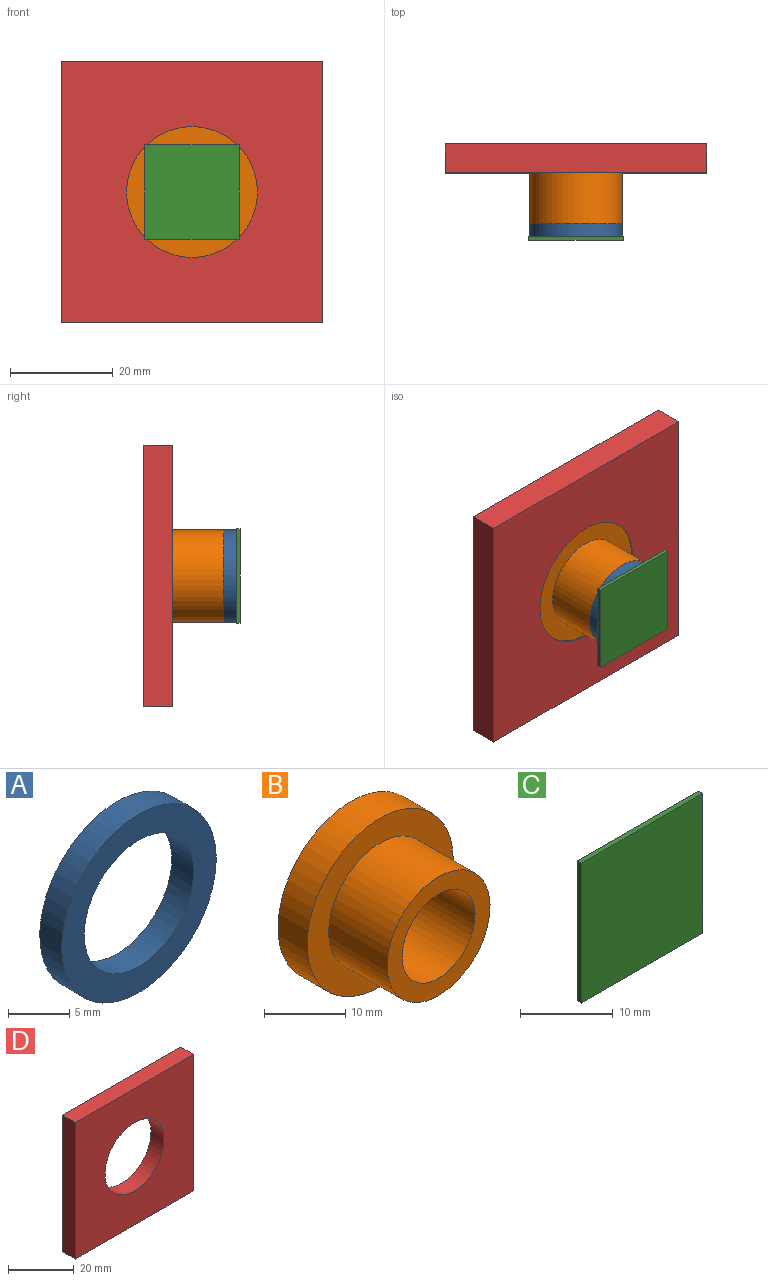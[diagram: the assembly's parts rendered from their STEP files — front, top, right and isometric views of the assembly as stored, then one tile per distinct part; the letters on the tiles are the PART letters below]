
ASSEMBLY  parts=4 mates=2
PART A: 4 faces, bbox 17.9x2.5x17.9 mm
  f0: cylinder r=6.35mm len=12.7mm, axis (0,1,0), area 101.3mm2, adj f2,f3
  f1: cylinder r=8.95mm len=17.91mm, axis (0,1,0), area 142.9mm2, adj f2,f3
  f2: plane 17.91x17.91mm, normal (0,-1,0), area 125.2mm2, adj f0,f1
  f3: plane 17.91x17.91mm, normal (0,1,0), area 125.2mm2, adj f0,f1
PART B: 6 faces, bbox 25.4x15.2x25.4 mm
  f0: cylinder r=12.7mm len=25.4mm, axis (0,1,0), area 405.4mm2, adj f1,f2
  f1: plane 25.4x25.4mm, normal (0,-1,0), area 254.9mm2, adj f0,f4
  f2: plane 25.4x25.4mm, normal (0,1,0), area 380mm2, adj f0,f3
  f3: cylinder r=6.35mm len=15.24mm, axis (0,1,0), area 608mm2, adj f2,f5
  f4: cylinder r=8.95mm len=17.91mm, axis (0,1,0), area 571.6mm2, adj f1,f5
  f5: plane 17.91x17.91mm, normal (0,-1,0), area 125.2mm2, adj f3,f4
PART C: 6 faces, bbox 18.4x0.6x18.4 mm
  f0: plane 18.42x0.64mm, normal (1,0,0), area 11.7mm2, adj f1,f3,f4,f5
  f1: plane 18.42x0.64mm, normal (0,0,1), area 11.7mm2, adj f0,f2,f4,f5
  f2: plane 18.42x0.64mm, normal (-1,0,0), area 11.7mm2, adj f1,f3,f4,f5
  f3: plane 18.42x0.64mm, normal (0,0,-1), area 11.7mm2, adj f0,f2,f4,f5
  f4: plane 18.42x18.42mm, normal (0,-1,0), area 339.1mm2, adj f0,f1,f2,f3
  f5: plane 18.42x18.42mm, normal (0,1,0), area 339.1mm2, adj f0,f1,f2,f3
PART D: 7 faces, bbox 50.8x5.6x50.8 mm
  f0: plane 50.8x5.59mm, normal (1,0,0), area 283.9mm2, adj f1,f3,f5,f6
  f1: plane 50.8x5.59mm, normal (0,0,1), area 283.9mm2, adj f0,f2,f5,f6
  f2: plane 50.8x5.59mm, normal (-1,0,0), area 283.9mm2, adj f1,f3,f5,f6
  f3: plane 50.8x5.59mm, normal (0,0,-1), area 283.9mm2, adj f0,f2,f5,f6
  f4: cylinder r=12.7mm len=25.4mm, axis (0,1,0), area 445.9mm2, adj f5,f6
  f5: plane 50.8x50.8mm, normal (0,-1,0), area 2073.9mm2, adj f0,f1,f2,f3,f4
  f6: plane 50.8x50.8mm, normal (0,1,0), area 2073.9mm2, adj f0,f1,f2,f3,f4
PLACE A t=(-0.02,8.87,-0.01)mm
PLACE B t=(-0.02,8.87,-0.01)mm
PLACE C t=(-0.02,-8.91,-0.01)mm
PLACE D t=(-0.02,9.12,-0.01)mm
MATE planar D.f4 <-> B.f0  axis (0,1,0) through (-0.02,6.33,-0.01)mm
MATE planar C.f5 <-> A.f1  axis (0,1,0) through (-0.02,-8.91,-0.01)mm
